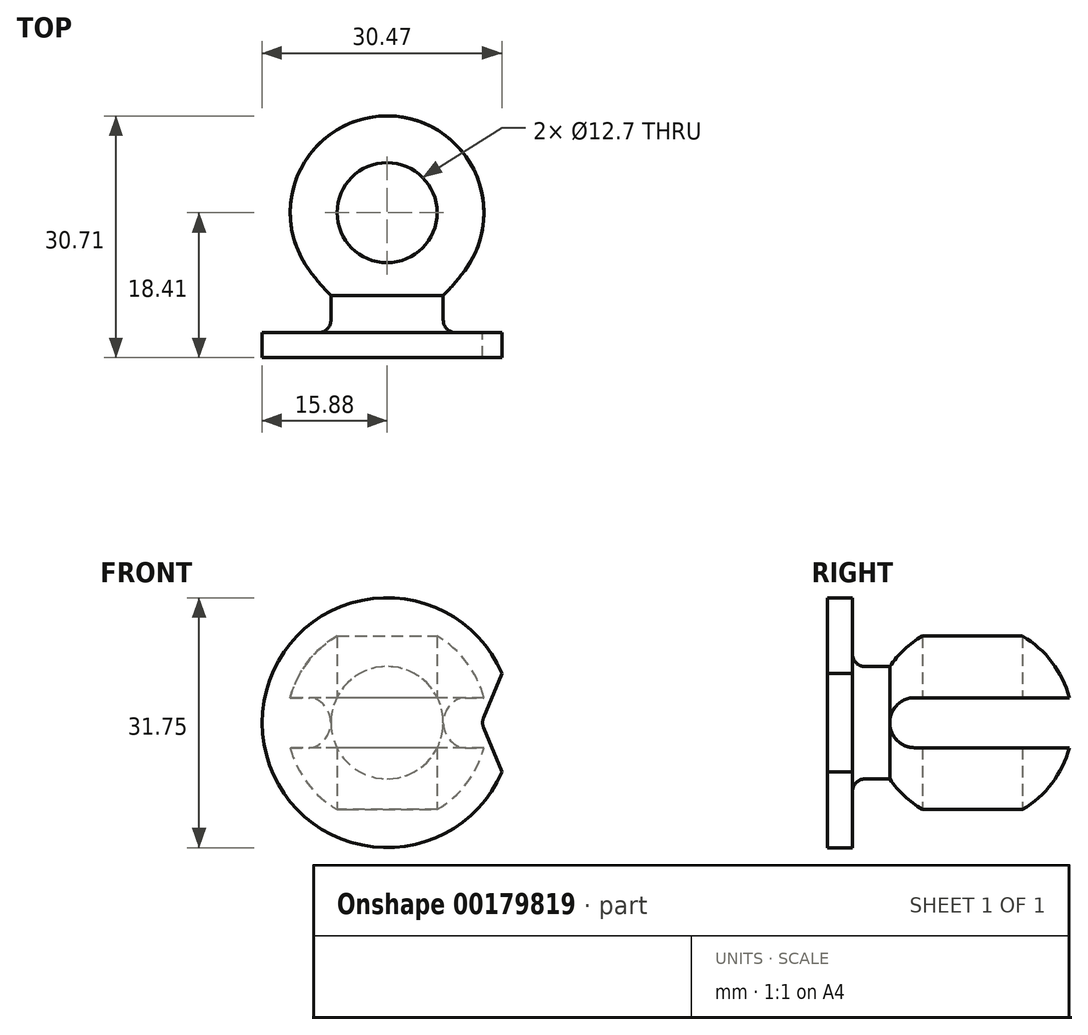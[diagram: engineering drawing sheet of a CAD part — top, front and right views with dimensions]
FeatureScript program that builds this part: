
annotation { "Feature Type Name" : "Feature", "Feature Type Description" : "" }
export const myFeature = defineFeature(function(context is Context, id is Id, definition is map)
    precondition{}
    {
        {
            var Q0;
            Q0=qCreatedBy(makeId("Front.planeOp"),FACE);
            var sketch = newSketch(context, id + "F0", { "sketchPlane" : qUnion([Q0])});
            skArc(sketch, "E0", {"start": v(0, -12.7) * mm, "mid": v(12.7, 0) * mm, "end": v(0, 12.7) * mm});
            skLineSegment(sketch, "E1", {"start": v(0, 12.7) * mm, "end": v(0, -12.7) * mm});
            skPoint(sketch, "E2.orphan", {"position": v(0, 15.18) * mm});
            skSolve(sketch);
        }
        {
            var Q0;
            Q0=qCreatedBy(makeId("Top.planeOp"),FACE);
            var sketch = newSketch(context, id + "F1", { "sketchPlane" : qUnion([Q0])});
            skCircle(sketch, "E3", {"center": v(0, 0) * mm, "radius": 6.35 * mm});
            skSolve(sketch);
        }
        {
            var Q0;
            Q0 = qSketchRegion(id + "F1", true);
            extrude(context, id + "F2", {"entities" : qUnion([Q0]), "endBound" : BoundingType.SYMMETRIC, "depth" : 25.4 * mm});
        }
        {
            var Q0;
            Q0=makeQuery(id+"F0.imprint","IMPRINT",FACE,{"disambiguationData":[TD([[makeQuery(id+"F0.imprint","IMPRINT",EDGE,{"derivedFrom":sQuery(id+"F0.wireOp",EDGE,"E0")}),1.0]])]});
            var Q1;
            Q1=makeQuery(id+"F2.opExtrude","SWEPT_FACE",FACE,{"disambiguationData":[OSD([sQuery(id+"F1.wireOp",EDGE,"E3")])]});
            revolve(context, id + "F3", {"entities" : qUnion([Q0]), "axis" : qUnion([Q1]), "revolveType" : RevolveType.FULL});
        }
        {
            var Q0;
            Q0=makeQuery(id+"F2.opExtrude","SWEPT_BODY",BODY,{"disambiguationData":[OSD([sQuery(id+"F1.wireOp",EDGE,"E3")])]});
            var Q1;
            Q1=makeQuery(id+"F3.opRevolve","SWEPT_BODY",BODY,{"disambiguationData":[OSD([sQuery(id+"F0.wireOp",EDGE,"E0"),sQuery(id+"F0.wireOp",EDGE,"E1")])]});
            booleanBodies(context, id + "F4", {"operationType" : BooleanOperationType.SUBTRACTION, "tools" : qUnion([Q0]), "targets" : qUnion([Q1])});
        }
        {
            var Q0;
            Q0=qCreatedBy(makeId("Front.planeOp"),FACE);
            var sketch = newSketch(context, id + "F5", { "sketchPlane" : qUnion([Q0])});
            skCircle(sketch, "E4", {"center": v(0, 0) * mm, "radius": 15.88 * mm});
            skSolve(sketch);
        }
        {
            var Q0;
            Q0 = qSketchRegion(id + "F5", true);
            extrude(context, id + "F6", {"entities" : qUnion([Q0]), "depth" : 3.17 * mm});
        }
        {
            var Q0;
            Q0=makeQuery(id+"F6.opExtrude","SWEPT_BODY",BODY,{"disambiguationData":[OSD([sQuery(id+"F5.wireOp",EDGE,"E4")])]});
            transform(context, id + "F7", {"entities" : qUnion([Q0]), "transformType" : TransformType.TRANSLATION_3D, "dx" : 0 * mm, "dy" : -15.24 * mm, "dz" : 0 * mm, "makeCopy" : false});
        }
        {
            var Q0;
            Q0=makeQuery(id+"F6.opExtrude","CAP_FACE",FACE,{"disambiguationData":[OSD([sQuery(id+"F5.wireOp",EDGE,"E4")])],"isStart":false});
            var sketch = newSketch(context, id + "F8", { "sketchPlane" : qUnion([Q0])});
            skCircle(sketch, "E5", {"center": v(0, 0) * mm, "radius": 7.14 * mm});
            skSolve(sketch);
        }
        {
            var Q0;
            Q0 = qSketchRegion(id + "F8", true);
            extrude(context, id + "F9", {"entities" : qUnion([Q0]), "depth" : 7.95 * mm});
        }
        {
            var Q0;
            Q0=makeQuery(id+"F9.opExtrude","SWEPT_BODY",BODY,{"disambiguationData":[OSD([sQuery(id+"F8.wireOp",EDGE,"E5")])]});
            transform(context, id + "F10", {"entities" : qUnion([Q0]), "transformType" : TransformType.TRANSLATION_3D, "dx" : 0 * mm, "dy" : 7.95 * mm, "dz" : 0 * mm, "makeCopy" : false});
        }
        {
            var Q0;
            Q0=makeQuery(id+"F3.opRevolve","SWEPT_BODY",BODY,{"disambiguationData":[OSD([sQuery(id+"F0.wireOp",EDGE,"E0"),sQuery(id+"F0.wireOp",EDGE,"E1")])]});
            var Q1;
            Q1=makeQuery(id+"F6.opExtrude","SWEPT_BODY",BODY,{"disambiguationData":[OSD([sQuery(id+"F5.wireOp",EDGE,"E4")])]});
            var Q2;
            Q2=makeQuery(id+"F9.opExtrude","SWEPT_BODY",BODY,{"disambiguationData":[OSD([sQuery(id+"F8.wireOp",EDGE,"E5")])]});
            booleanBodies(context, id + "F11", {"operationType" : BooleanOperationType.UNION, "tools" : qUnion([Q0, Q1, Q2])});
        }
        {
            var Q0;
            Q0=qCreatedBy(makeId("Right.planeOp"),FACE);
            var sketch = newSketch(context, id + "F12", { "sketchPlane" : qUnion([Q0])});
            skLineSegment(sketch, "E6.bottom", {"start": v(-7.33, 3.18) * mm, "end": v(27.6, 3.18) * mm});
            skLineSegment(sketch, "E6.top", {"start": v(-7.33, -3.18) * mm, "end": v(27.6, -3.18) * mm});
            skLineSegment(sketch, "E6.right", {"start": v(27.6, 3.18) * mm, "end": v(27.6, -3.18) * mm});
            skArc(sketch, "E7", {"start": v(-7.33, 3.17) * mm, "mid": v(-10.5, 0) * mm, "end": v(-7.33, -3.18) * mm});
            skSolve(sketch);
        }
        {
            var Q0;
            Q0 = qSketchRegion(id + "F12", true);
            extrude(context, id + "F13", {"entities" : qUnion([Q0]), "endBound" : BoundingType.SYMMETRIC, "depth" : 50.8 * mm});
        }
        {
            var Q0;
            Q0=makeQuery(id+"F13.opExtrude","SWEPT_BODY",BODY,{"disambiguationData":[OSD([sQuery(id+"F12.wireOp",EDGE,"E6.bottom"),sQuery(id+"F12.wireOp",EDGE,"E6.top"),sQuery(id+"F12.wireOp",EDGE,"E6.right"),sQuery(id+"F12.wireOp",EDGE,"E7")])]});
            var Q1;
            Q1=makeQuery(id+"F3.opRevolve","SWEPT_BODY",BODY,{"disambiguationData":[OSD([sQuery(id+"F0.wireOp",EDGE,"E0"),sQuery(id+"F0.wireOp",EDGE,"E1")])]});
            booleanBodies(context, id + "F14", {"operationType" : BooleanOperationType.SUBTRACTION, "tools" : qUnion([Q0]), "targets" : qUnion([Q1])});
        }
        {
            var Q0;
            Q0=makeQuery(id+"F11.opBoolean","INTERSECT",EDGE,{"derivedFrom":[makeQuery(id+"F6.opExtrude","CAP_FACE",FACE,{"disambiguationData":[OSD([sQuery(id+"F5.wireOp",EDGE,"E4")])],"isStart":true}),makeQuery(id+"F9.opExtrude","SWEPT_FACE",FACE,{"disambiguationData":[OSD([sQuery(id+"F8.wireOp",EDGE,"E5")])]})]});
            fillet(context, id + "F15", {"entities" : qUnion([Q0]), "radius" : 1.59 * mm, "tangentPropagation" : true, "allowEdgeOverflow" : false});
        }
        {
            var Q0;
            Q0=makeQuery(id+"F6.opExtrude","CAP_FACE",FACE,{"disambiguationData":[OSD([sQuery(id+"F5.wireOp",EDGE,"E4")])],"isStart":false});
            var sketch = newSketch(context, id + "F16", { "sketchPlane" : qUnion([Q0])});
            skPoint(sketch, "E8.start.orphan", {"position": v(0, 0) * mm});
            skLineSegment(sketch, "E9.MirrorCS", {"start": v(12.25, 0.6) * mm, "end": v(17.81, 14.03) * mm});
            skLineSegment(sketch, "E10.MirrorCS", {"start": v(17.81, 14.03) * mm, "end": v(17.81, -14.03) * mm});
            skArc(sketch, "E11.MirrorCS", {"start": v(12.25, 0.6) * mm, "mid": v(12.13, 0) * mm, "end": v(12.25, -0.6) * mm});
            skLineSegment(sketch, "E12.MirrorCS", {"start": v(12.25, -0.6) * mm, "end": v(17.81, -14.03) * mm});
            skSolve(sketch);
        }
        {
            var Q0;
            Q0 = qSketchRegion(id + "F16", true);
            extrude(context, id + "F17", {"entities" : qUnion([Q0]), "endBound" : BoundingType.SYMMETRIC, "depth" : 6.35 * mm});
        }
        {
            var Q0;
            Q0=makeQuery(id+"F17.opExtrude","SWEPT_BODY",BODY,{"disambiguationData":[OSD([sQuery(id+"F16.wireOp",EDGE,"73158e47-27a5-46bf-a657-c8c149ad69210.MirrorCS"),sQuery(id+"F16.wireOp",EDGE,"6fe4a66c-1736-4806-945b-af24c14ed8630.MirrorCS"),sQuery(id+"F16.wireOp",EDGE,"6d5ff9a2-e50b-4ebb-aac7-ae897bb5c4350.MirrorCS"),sQuery(id+"F16.wireOp",EDGE,"824f3bdc-c73a-479e-ab19-50ac140facd90.MirrorCS")])]});
            var Q1;
            Q1=makeQuery(id+"F17.opExtrude","SWEPT_BODY",BODY,{"disambiguationData":[OSD([sQuery(id+"F16.wireOp",EDGE,"E9.MirrorCS"),sQuery(id+"F16.wireOp",EDGE,"E10.MirrorCS"),sQuery(id+"F16.wireOp",EDGE,"E11.MirrorCS"),sQuery(id+"F16.wireOp",EDGE,"E12.MirrorCS")])]});
            var Q2;
            Q2=makeQuery(id+"F3.opRevolve","SWEPT_BODY",BODY,{"disambiguationData":[OSD([sQuery(id+"F0.wireOp",EDGE,"E0"),sQuery(id+"F0.wireOp",EDGE,"E1")])]});
            booleanBodies(context, id + "F18", {"operationType" : BooleanOperationType.SUBTRACTION, "tools" : qUnion([Q0, Q1]), "targets" : qUnion([Q2])});
        }
    });
